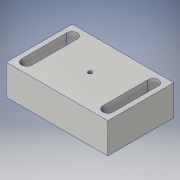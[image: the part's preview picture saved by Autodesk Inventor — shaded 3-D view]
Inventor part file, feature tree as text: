
AUTODESK INVENTOR PART (.ipt)
format: ipt  version: 2016 (Build 200138000, 138)  size: 126,464 bytes
history: native  units: in
note: dims shown in document units (in); Inventor stores cm internally (conversion verified against a paired STEP export)
features: sketch x3, extrude x2, hole x1
ambient origin geometry x8: Origin, YZ Plane, XZ Plane, XY Plane, X Axis, Y Axis, Z Axis, Center Point
bodies: Solid1 (feature_tree)
feature tree (6):
  extrude  "Extrusion1"  Depth=2.5in
  hole  "Hole1"  [1 undecoded]
  extrude  "Extrusion2"  Depth=0.26in
  sketch  "Sketch1"  dims[d0=1.625in d1=0.0in d2=2.5in]
  sketch  "Sketch2"  dims[d3=0.75in d4=0.8125in]
  sketch  "Sketch3"  dims[d5=1.25in d6=0.097in d7=0.5in d8=0.375in d9=0.25in d10=0.5635in d11=0.5in d12=0.8108in d13=0.26in d15=0.125in d16=0.125in d17=1.0in d18=1.0in d19=0.0in]
note: 1 required parameter value undecoded (feature->parameter linkage not recoverable at this tier; creation-order binding heuristic only, values carry confidence <= 0.55)
